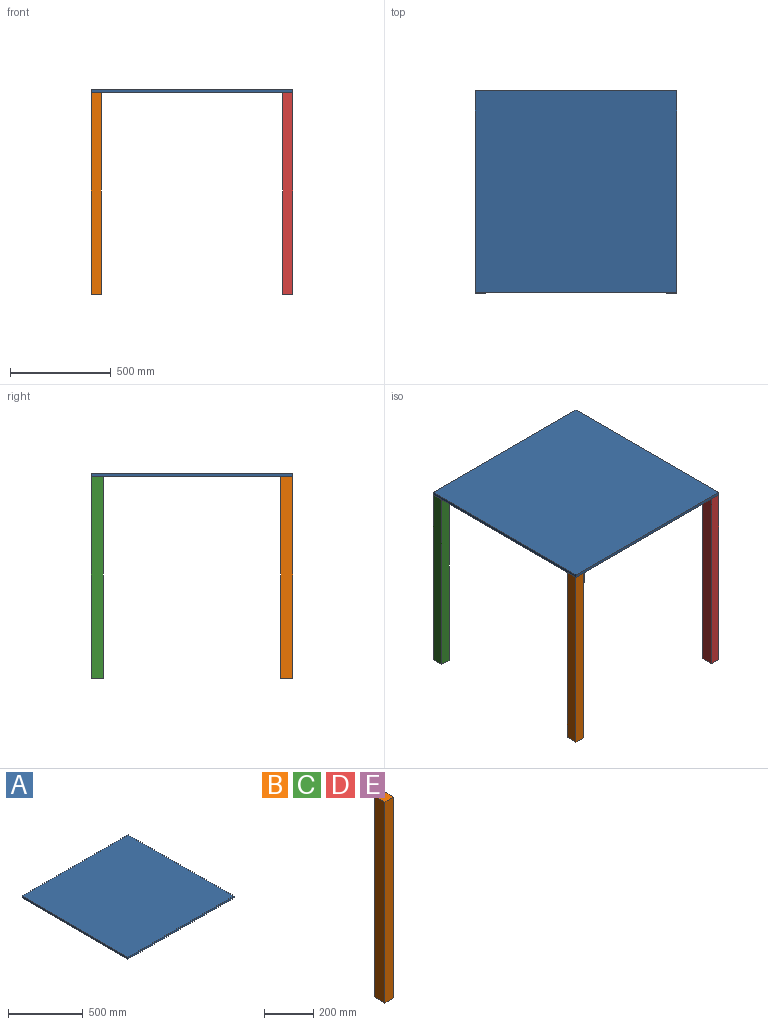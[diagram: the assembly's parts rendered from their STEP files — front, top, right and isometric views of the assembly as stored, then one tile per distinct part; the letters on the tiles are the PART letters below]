
ASSEMBLY  parts=5 mates=5
PART A: 6 faces, bbox 1000x1000x15 mm
  f0: plane 1000x15mm, normal (0,1,0), area 15000mm2, adj f1,f3,f4,f5
  f1: plane 1000x15mm, normal (-1,0,0), area 15000mm2, adj f0,f2,f4,f5
  f2: plane 1000x15mm, normal (0,-1,0), area 15000mm2, adj f1,f3,f4,f5
  f3: plane 1000x15mm, normal (1,0,0), area 15000mm2, adj f0,f2,f4,f5
  f4: plane 1000x1000mm, normal (0,0,1), area 1000000mm2, adj f0,f1,f2,f3
  f5: plane 1000x1000mm, normal (0,0,-1), area 1000000mm2, adj f0,f1,f2,f3
PART B: 6 faces, bbox 50x60x1000 mm
  f0: plane 1000x60mm, normal (-1,0,0), area 60000mm2, adj f1,f3,f4,f5
  f1: plane 1000x50mm, normal (0,-1,0), area 50000mm2, adj f0,f2,f4,f5
  f2: plane 1000x60mm, normal (1,0,0), area 60000mm2, adj f1,f3,f4,f5
  f3: plane 1000x50mm, normal (0,1,0), area 50000mm2, adj f0,f2,f4,f5
  f4: plane 60x50mm, normal (0,0,1), area 3000mm2, adj f0,f1,f2,f3
  f5: plane 60x50mm, normal (0,0,-1), area 3000mm2, adj f0,f1,f2,f3
PART C: same geometry as B
PART D: same geometry as B
PART E: same geometry as B
PLACE A t=(223.54,372.39,404.15)mm
PLACE B t=(71.72,260.31,-95.85)mm
PLACE C t=(71.72,1200.31,-95.85)mm
PLACE D t=(1021.72,260.31,-95.85)mm
PLACE E t=(1021.72,1200.31,-95.85)mm
MATE fastened D.f4 <-> A.f5  axis (0,0,1) through (1071.72,260.31,404.15)mm
MATE pin_slot B.f4 <-> B.f4  axis (0,0,1) through (96.72,290.31,404.15)mm
MATE fastened C.f4 <-> A.f5  axis (0,0,1) through (71.72,1260.31,404.15)mm
MATE fastened E.f4 <-> A.f5  axis (0,0,1) through (1071.72,1260.31,404.15)mm
MATE fastened B.f4 <-> A.f5  axis (0,0,1) through (71.72,260.31,404.15)mm
